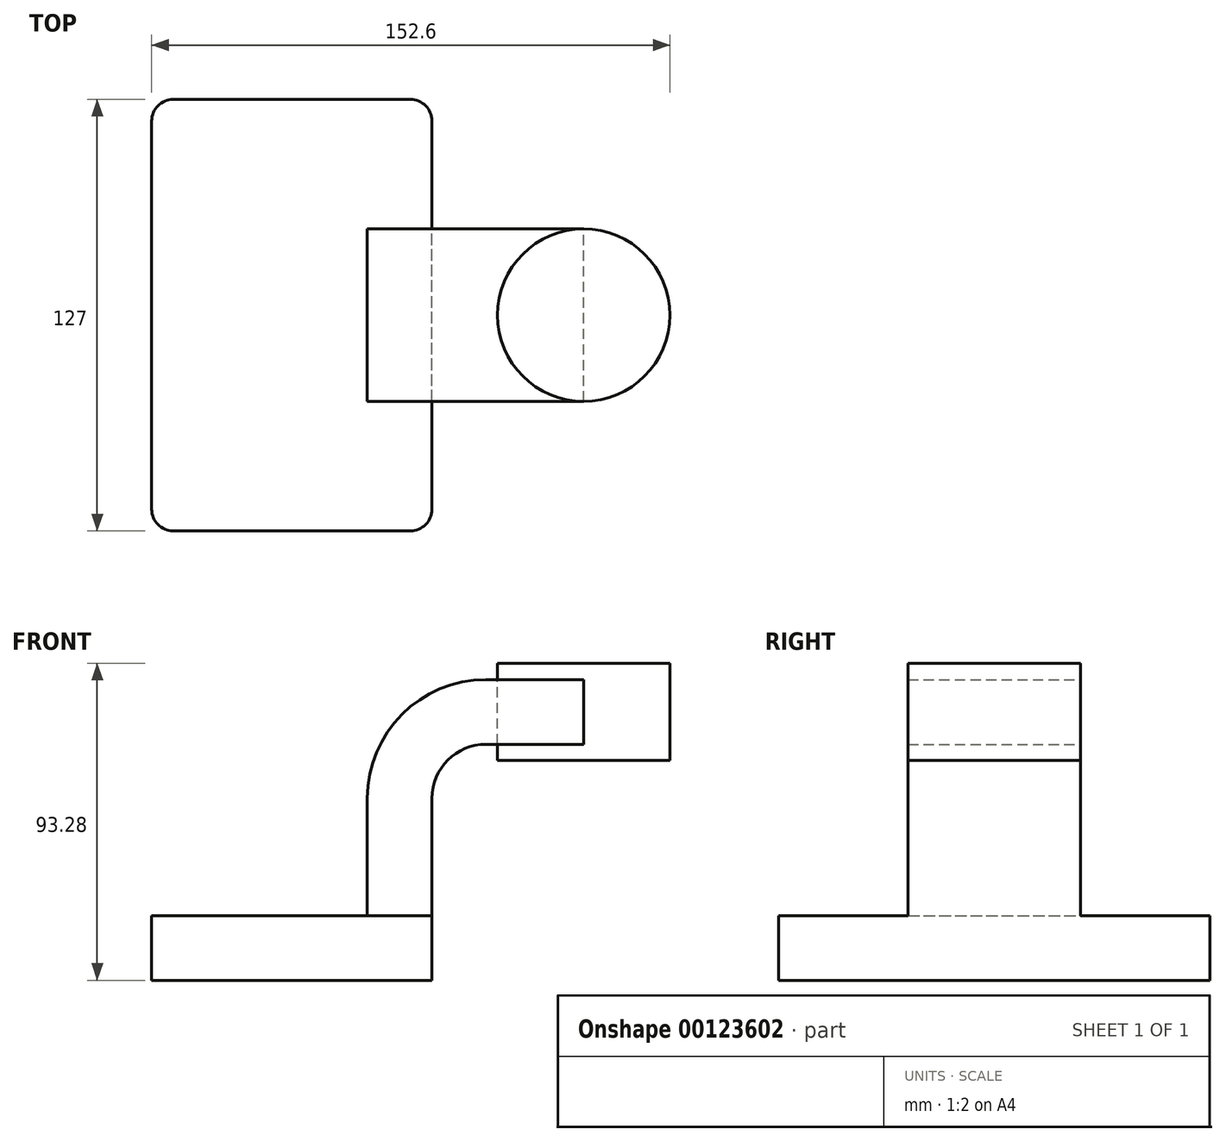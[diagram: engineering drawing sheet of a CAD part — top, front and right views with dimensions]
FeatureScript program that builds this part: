
annotation { "Feature Type Name" : "Feature", "Feature Type Description" : "" }
export const myFeature = defineFeature(function(context is Context, id is Id, definition is map)
    precondition{}
    {
        {
            var Q0;
            Q0=qCreatedBy(makeId("Front.planeOp"),FACE);
            var sketch = newSketch(context, id + "F0", { "sketchPlane" : qUnion([Q0])});
            skLineSegment(sketch, "E0.bottom", {"start": v(41.27, 9.53) * mm, "end": v(-41.28, 9.53) * mm});
            skLineSegment(sketch, "E0.top", {"start": v(41.28, -9.52) * mm, "end": v(-41.27, -9.52) * mm});
            skLineSegment(sketch, "E0.left", {"start": v(41.27, 9.53) * mm, "end": v(41.28, -9.52) * mm});
            skLineSegment(sketch, "E0.right", {"start": v(-41.28, 9.53) * mm, "end": v(-41.27, -9.52) * mm});
            skPoint(sketch, "E0.middle", {"position": v(0, 0) * mm});
            skLineSegment(sketch, "E1.bottom", {"start": v(111.33, 55.17) * mm, "end": v(60.53, 55.17) * mm});
            skLineSegment(sketch, "E1.top", {"start": v(111.33, 83.75) * mm, "end": v(60.53, 83.75) * mm});
            skLineSegment(sketch, "E1.left", {"start": v(111.33, 55.17) * mm, "end": v(111.33, 83.75) * mm});
            skLineSegment(sketch, "E1.right", {"start": v(60.53, 55.17) * mm, "end": v(60.53, 83.75) * mm});
            skPoint(sketch, "E1.middle", {"position": v(85.93, 69.46) * mm});
            skLineSegment(sketch, "E2", {"start": v(41.27, 9.53) * mm, "end": v(41.27, 44.06) * mm});
            skArc(sketch, "E3", {"start": v(41.27, 44.06) * mm, "mid": v(45.92, 55.29) * mm, "end": v(57.15, 59.94) * mm});
            skLineSegment(sketch, "E4", {"start": v(57.15, 59.94) * mm, "end": v(85.93, 59.94) * mm});
            skLineSegment(sketch, "E5.0", {"start": v(57.15, 78.99) * mm, "end": v(85.93, 78.99) * mm});
            skArc(sketch, "E5.1", {"start": v(22.22, 44.06) * mm, "mid": v(32.45, 68.76) * mm, "end": v(57.15, 78.99) * mm});
            skLineSegment(sketch, "E5.2", {"start": v(22.22, 9.53) * mm, "end": v(22.22, 44.06) * mm});
            skLineSegment(sketch, "E6", {"start": v(85.93, 78.99) * mm, "end": v(85.93, 59.94) * mm});
            skFitSpline(sketch, "E7", {"points": [v(-41.28, 9.53) * mm, v(57.15, 78.99) * mm], "startDerivative": vector(37.27, 105.77) * mm, "endDerivative": vector(153.34, -14.67) * mm});
            skLineSegment(sketch, "E8", {"start": v(85.93, 83.75) * mm, "end": v(85.93, 55.17) * mm});
            skSolve(sketch);
        }
        {
            var Q0;
            Q0=makeQuery(id+"F0.imprint","IMPRINT",FACE,{"disambiguationData":[TD([[makeQuery(id+"F0.imprint","IMPRINT",EDGE,{"derivedFrom":sQuery(id+"F0.wireOp",EDGE,"E0.top")}),-1.0]])]});
            extrude(context, id + "F1", {"entities" : qUnion([Q0]), "endBound" : BoundingType.SYMMETRIC, "depth" : 127 * mm});
        }
        {
            var Q0;
            {var subQ1=sQuery(id+"F0.wireOp",EDGE,"E2");Q0=makeQuery(id+"F0.imprint","IMPRINT",FACE,{"disambiguationData":[TD([[makeQuery(id+"F0.imprint","IMPRINT",EDGE,{"derivedFrom":subQ1}),1.0]])]});}
            var Q1;
            {var subQ5=sQuery(id+"F0.wireOp",EDGE,"E6");Q1=makeQuery(id+"F0.imprint","IMPRINT",FACE,{"disambiguationData":[TD([[makeQuery(id+"F0.imprint","IMPRINT",EDGE,{"derivedFrom":subQ5}),-1.0]])]});}
            var Q2;
            {var subQ0=sQuery(id+"F0.wireOp",EDGE,"E4");var subQ1=sQuery(id+"F0.wireOp",EDGE,"E1.right");var subQ2=makeQuery(id+"F0.imprint","INTERSECT",VERTEX,{"derivedFrom":[subQ1,subQ0]});Q2=makeQuery(id+"F0.imprint","IMPRINT",FACE,{"disambiguationData":[TD([[makeQuery(id+"F0.imprint","IMPRINT",EDGE,{"disambiguationData":[TD([[subQ2,-1.0]])],"derivedFrom":subQ1}),-1.0]])]});}
            extrude(context, id + "F2", {"entities" : qUnion([Q0, Q1, Q2]), "operationType" : NewBodyOperationType.ADD, "endBound" : BoundingType.SYMMETRIC, "depth" : 50.8 * mm});
        }
        {
            var Q0;
            Q0=makeQuery(id+"F0.imprint","IMPRINT",FACE,{"disambiguationData":[TD([[makeQuery(id+"F0.imprint","IMPRINT",EDGE,{"derivedFrom":sQuery(id+"F0.wireOp",EDGE,"E5.1")}),1.0]])]});
            extrude(context, id + "F3", {"entities" : qUnion([Q0]), "operationType" : NewBodyOperationType.ADD, "endBound" : BoundingType.SYMMETRIC, "depth" : 15.88 * mm});
        }
        {
            var Q0;
            {var subQ0=sQuery(id+"F0.wireOp",EDGE,"E1.left");Q0=makeQuery(id+"F0.imprint","IMPRINT",FACE,{"disambiguationData":[TD([[makeQuery(id+"F0.imprint","IMPRINT",EDGE,{"derivedFrom":subQ0}),1.0]])]});}
            var Q1;
            Q1=sQuery(id+"F0.wireOp",EDGE,"E8");
            revolve(context, id + "F4", {"entities" : qUnion([Q0]), "axis" : qUnion([Q1]), "revolveType" : RevolveType.FULL});
        }
        {
            var Q0;
            Q0=makeQuery(id+"F1.opExtrude","CAP_EDGE",EDGE,{"disambiguationData":[OSD([sQuery(id+"F0.wireOp",EDGE,"E0.left")])],"isStart":false});
            var Q1;
            Q1=makeQuery(id+"F1.opExtrude","CAP_EDGE",EDGE,{"disambiguationData":[OSD([sQuery(id+"F0.wireOp",EDGE,"E0.right")])],"isStart":false});
            var Q2;
            Q2=makeQuery(id+"F1.opExtrude","CAP_EDGE",EDGE,{"disambiguationData":[OSD([sQuery(id+"F0.wireOp",EDGE,"E0.right")])],"isStart":true});
            var Q3;
            Q3=makeQuery(id+"F1.opExtrude","CAP_EDGE",EDGE,{"disambiguationData":[OSD([sQuery(id+"F0.wireOp",EDGE,"E0.left")])],"isStart":true});
            fillet(context, id + "F5", {"entities" : qUnion([Q0, Q1, Q2, Q3]), "radius" : 6.35 * mm, "tangentPropagation" : true, "allowEdgeOverflow" : false});
        }
    });
